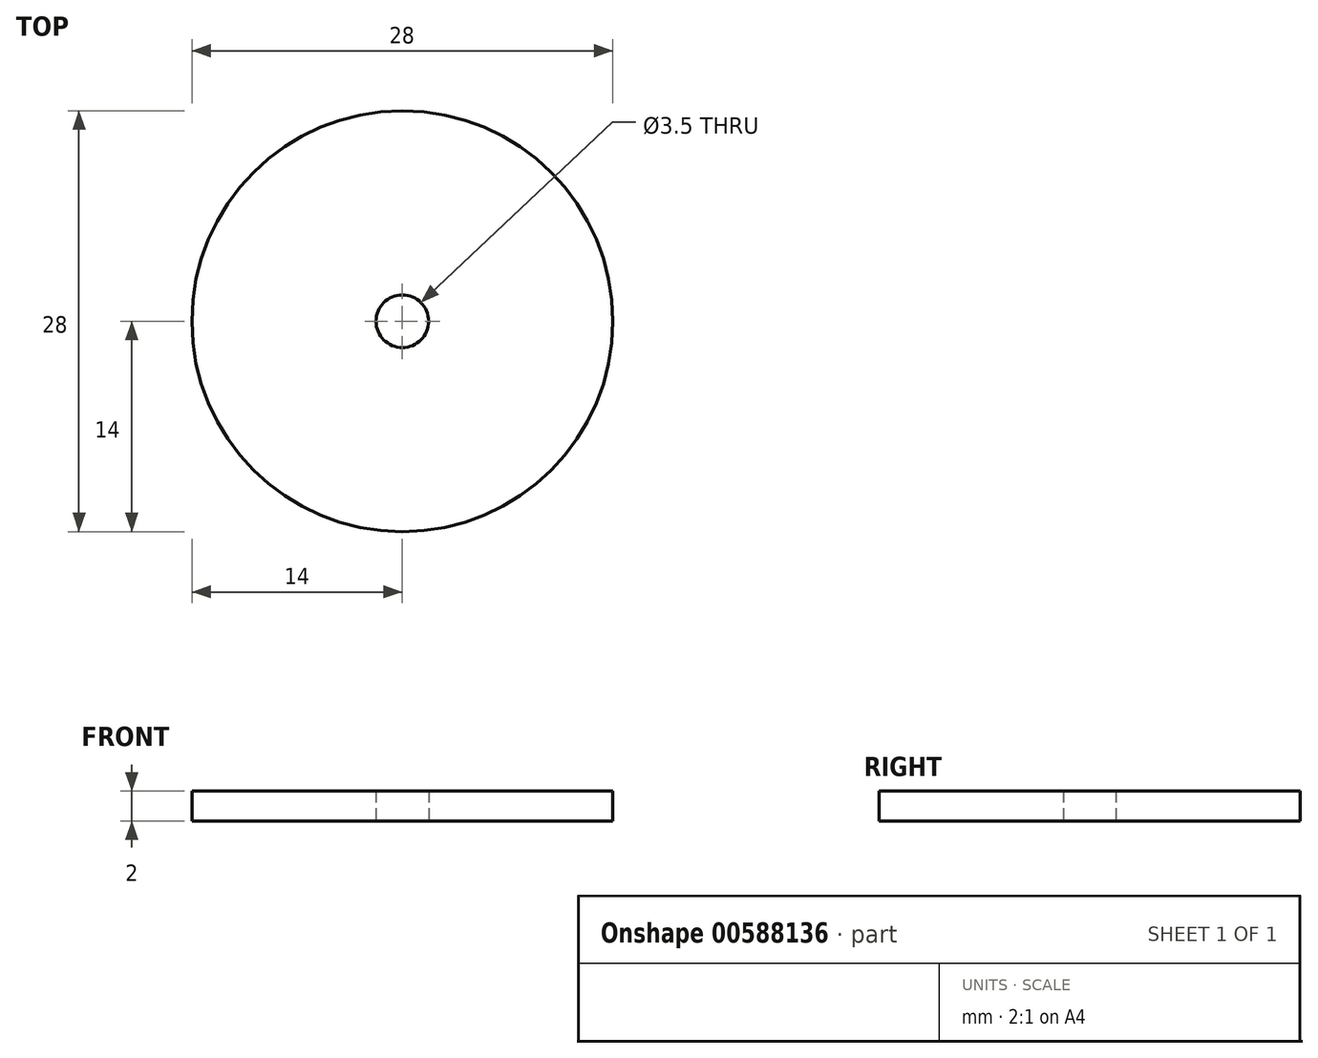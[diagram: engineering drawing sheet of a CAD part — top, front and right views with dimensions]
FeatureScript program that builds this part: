
annotation { "Feature Type Name" : "Feature", "Feature Type Description" : "" }
export const myFeature = defineFeature(function(context is Context, id is Id, definition is map)
    precondition{}
    {
        {
            var Q0;
            Q0=qCreatedBy(makeId("Front.planeOp"),FACE);
            var sketch = newSketch(context, id + "F0", { "sketchPlane" : qUnion([Q0])});
            skLineSegment(sketch, "E0", {"start": v(0, 0) * mm, "end": v(0, 42) * mm});
            skArc(sketch, "E1", {"start": v(0, 42) * mm, "mid": v(15.81, 30.6) * mm, "end": v(10, 12) * mm});
            skArc(sketch, "E2", {"start": v(10, 12) * mm, "mid": v(7.68, 4.56) * mm, "end": v(14, 0) * mm});
            skLineSegment(sketch, "E3", {"start": v(14, 0) * mm, "end": v(1.75, 0) * mm});
            skLineSegment(sketch, "E4", {"start": v(1.75, 0) * mm, "end": v(1.75, 27) * mm});
            skLineSegment(sketch, "E5", {"start": v(1.75, 27) * mm, "end": v(0, 27) * mm});
            skLineSegment(sketch, "E6.top", {"start": v(14, -2) * mm, "end": v(1.75, -2) * mm});
            skLineSegment(sketch, "E6.left", {"start": v(14, 0) * mm, "end": v(14, -2) * mm});
            skLineSegment(sketch, "E6.right", {"start": v(1.75, 0) * mm, "end": v(1.75, -2) * mm});
            skSolve(sketch);
        }
        {
            var Q0;
            {var subQ0=sQuery(id+"F0.wireOp",EDGE,"E1");Q0=makeQuery(id+"F0.imprint","IMPRINT",FACE,{"disambiguationData":[TD([[makeQuery(id+"F0.imprint","IMPRINT",EDGE,{"derivedFrom":subQ0}),-1.0]])]});}
            var Q1;
            Q1=makeQuery(id+"F0.imprint","IMPRINT",FACE,{"disambiguationData":[TD([[makeQuery(id+"F0.imprint","IMPRINT",EDGE,{"derivedFrom":sQuery(id+"F0.wireOp",EDGE,"E3")}),1.0]])]});
            var Q2;
            Q2=sQuery(id+"F0.wireOp",EDGE,"E0");
            revolve(context, id + "F1", {"entities" : qUnion([Q0, Q1]), "axis" : qUnion([Q2]), "revolveType" : RevolveType.FULL});
        }
    });
